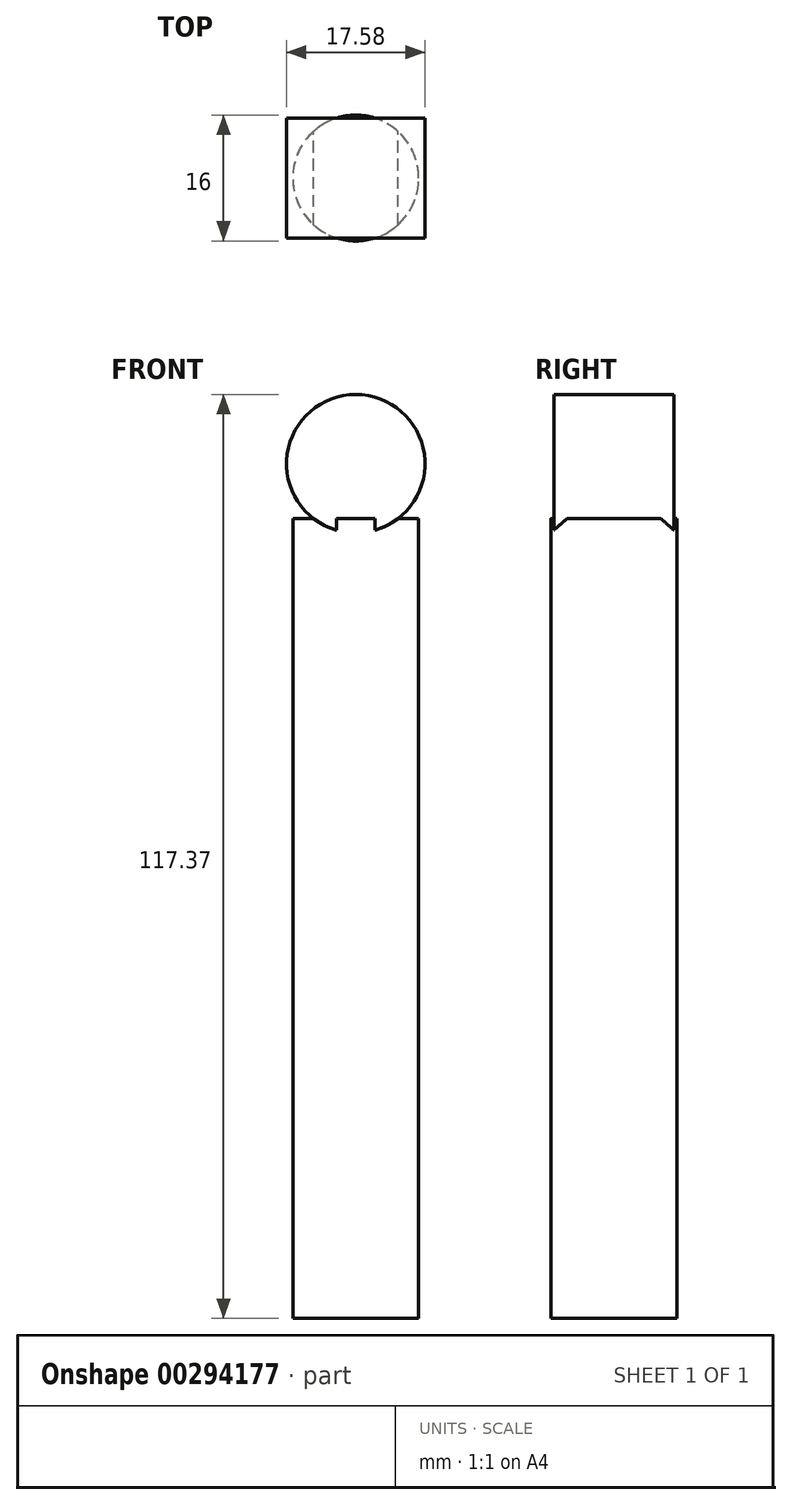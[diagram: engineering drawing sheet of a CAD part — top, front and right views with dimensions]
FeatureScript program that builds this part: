
annotation { "Feature Type Name" : "Feature", "Feature Type Description" : "" }
export const myFeature = defineFeature(function(context is Context, id is Id, definition is map)
    precondition{}
    {
        {
            var Q0;
            Q0=qCreatedBy(makeId("Top.planeOp"),FACE);
            var sketch = newSketch(context, id + "F0", { "sketchPlane" : qUnion([Q0])});
            skCircle(sketch, "E0", {"center": v(0, 0) * mm, "radius": 8 * mm});
            skSolve(sketch);
        }
        {
            var Q0;
            Q0=makeQuery(id+"F0.imprint","IMPRINT",FACE,{"disambiguationData":[TD([[makeQuery(id+"F0.imprint","IMPRINT",EDGE,{"derivedFrom":sQuery(id+"F0.wireOp",EDGE,"E0")}),1.0]])]});
            extrude(context, id + "F1", {"entities" : qUnion([Q0]), "depth" : 101.6 * mm});
        }
        {
            var Q0;
            Q0=qCreatedBy(makeId("Front.planeOp"),FACE);
            var sketch = newSketch(context, id + "F2", { "sketchPlane" : qUnion([Q0])});
            skCircle(sketch, "E1", {"center": v(0, 108.58) * mm, "radius": 8.79 * mm});
            skSolve(sketch);
        }
        {
            var Q0;
            Q0 = qSketchRegion(id + "F2", true);
            extrude(context, id + "F3", {"entities" : qUnion([Q0]), "operationType" : NewBodyOperationType.ADD, "endBound" : BoundingType.SYMMETRIC, "depth" : 15.24 * mm});
        }
    });
